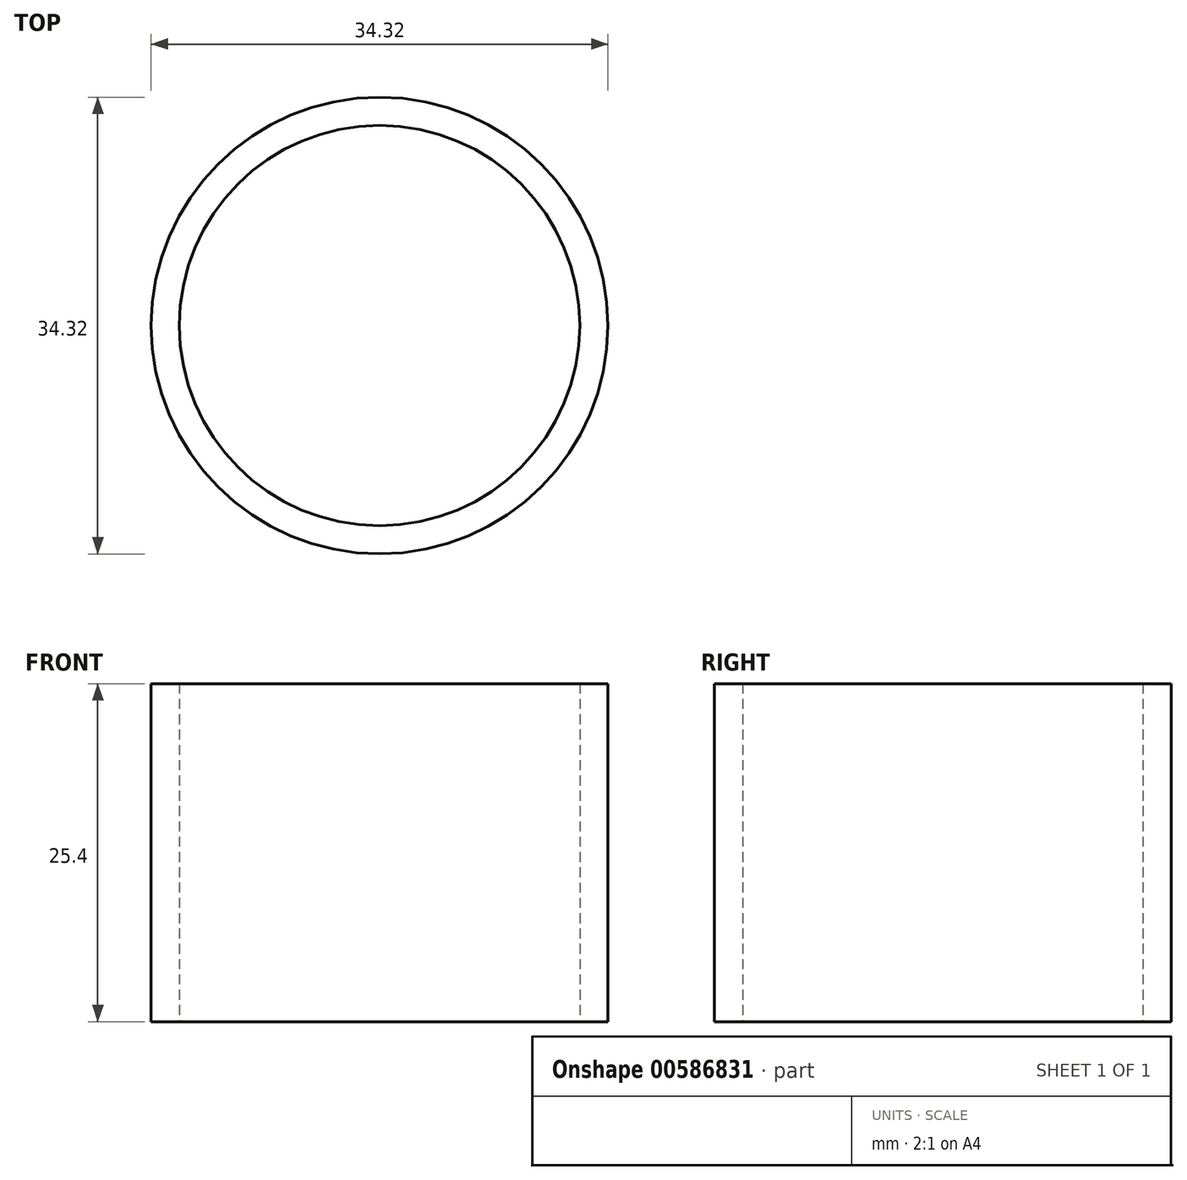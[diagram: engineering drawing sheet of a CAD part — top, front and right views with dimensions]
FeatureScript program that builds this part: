
annotation { "Feature Type Name" : "Feature", "Feature Type Description" : "" }
export const myFeature = defineFeature(function(context is Context, id is Id, definition is map)
    precondition{}
    {
        {
            var Q0;
            Q0=qCreatedBy(makeId("Top.planeOp"),FACE);
            var sketch = newSketch(context, id + "F0", { "sketchPlane" : qUnion([Q0])});
            skCircle(sketch, "E0", {"center": v(0, 0) * mm, "radius": 17.16 * mm});
            skCircle(sketch, "E1", {"center": v(0, 0) * mm, "radius": 15.04 * mm});
            skSolve(sketch);
        }
        {
            var Q0;
            Q0=makeQuery(id+"F0.imprint","IMPRINT",FACE,{"disambiguationData":[TD([[makeQuery(id+"F0.imprint","IMPRINT",EDGE,{"derivedFrom":sQuery(id+"F0.wireOp",EDGE,"E0")}),1.0]])]});
            extrude(context, id + "F1", {"entities" : qUnion([Q0]), "depth" : 25.4 * mm, "offsetDistance" : 25.4 * mm});
        }
    });
